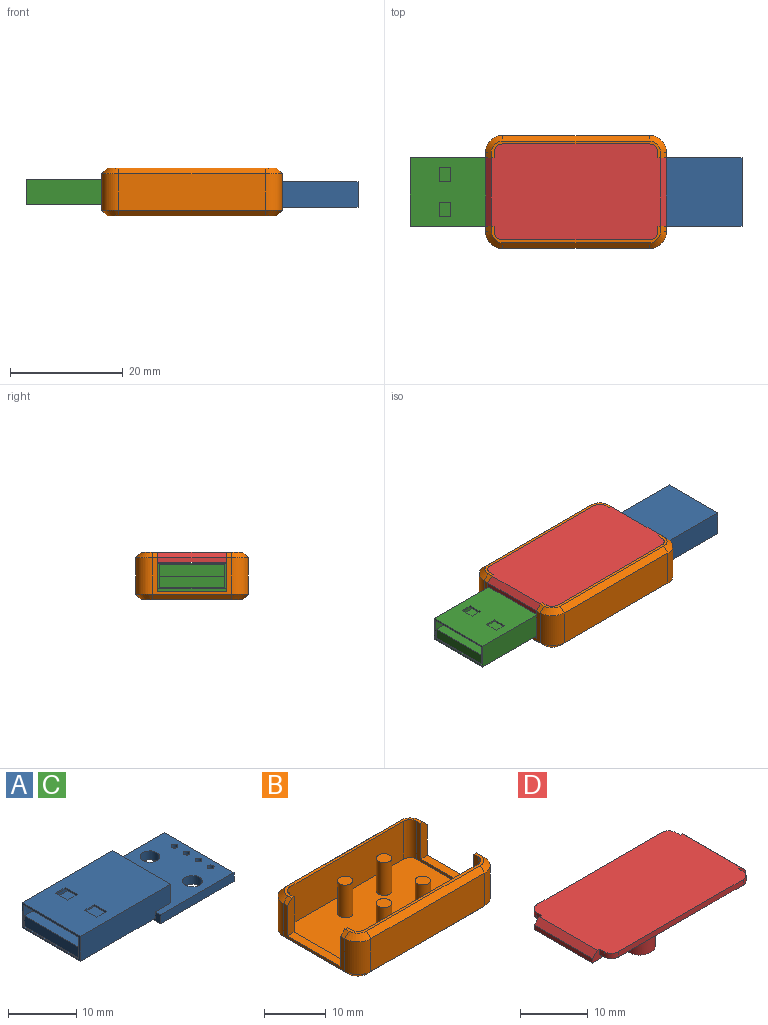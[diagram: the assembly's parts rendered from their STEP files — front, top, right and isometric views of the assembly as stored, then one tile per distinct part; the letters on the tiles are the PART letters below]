
ASSEMBLY  parts=4 mates=3
PART A: 33 faces, bbox 30.8x14.4x5 mm
  f0: plane 18.8x12.14mm, normal (0,0,1), area 218.2mm2, adj f2,f3,f4,f5,f25,f26,f27,f28
  f1: plane 17x11.54mm, normal (0,0,-1), area 186.2mm2, adj f2,f20,f21,f24,f25,f26,f27,f28
  f2: plane 12.14x4.5mm, normal (-1,0,0), area 9.6mm2, adj f0,f1,f3,f5,f6,f19,f20,f21
  f3: plane 18.8x4.5mm, normal (0,-1,0), area 80.9mm2, adj f0,f2,f4,f6,f8,f18
  f4: plane 12.14x3.35mm, normal (1,0,0), area 40.7mm2, adj f0,f3,f5,f18
  f5: plane 18.8x4.5mm, normal (0,1,0), area 80.9mm2, adj f0,f2,f4,f6,f8,f18
  f6: plane 15.56x12.14mm, normal (0,0,-1), area 188.9mm2, adj f2,f3,f5,f8
  f7: plane 15.24x1.6mm, normal (0,1,0), area 24.4mm2, adj f8,f15,f17,f18
  f8: plane 14.43x1.6mm, normal (-1,0,0), area 9.1mm2, adj f3,f5,f6,f7,f9,f17,f18
  f9: plane 15.24x1.6mm, normal (0,-1,0), area 24.4mm2, adj f8,f15,f17,f18
  f10: cylinder r=0.5mm len=1.6mm, axis (0,0,1), area 5mm2, adj f17,f18
  f11: cylinder r=0.5mm len=1.6mm, axis (0,0,1), area 5mm2, adj f17,f18
  f12: cylinder r=0.5mm len=1.6mm, axis (0,0,1), area 5mm2, adj f17,f18
  f13: cylinder r=1.45mm len=2.9mm, axis (0,0,1), area 14.6mm2, adj f17,f18
  f14: cylinder r=0.5mm len=1.6mm, axis (0,0,1), area 5mm2, adj f17,f18
  f15: plane 14.43x1.6mm, normal (1,0,0), area 23.1mm2, adj f7,f9,f17,f18
  f16: cylinder r=1.45mm len=2.9mm, axis (0,0,1), area 14.6mm2, adj f17,f18
  f17: plane 15.24x14.43mm, normal (0,0,-1), area 203.6mm2, adj f7,f8,f9,f10,f11,f12,f13,f14
  f18: plane 15.24x14.43mm, normal (0,0,1), area 164.2mm2, adj f3,f4,f5,f7,f8,f9,f10,f11
  f19: plane 11.54x0.2mm, normal (0,0,1), area 2.3mm2, adj f2,f20,f21,f22
  f20: plane 17x3.9mm, normal (0,1,0), area 34.4mm2, adj f1,f2,f19,f22,f23,f24
  f21: plane 17x3.9mm, normal (0,-1,0), area 34.4mm2, adj f1,f2,f19,f22,f23,f24
  f22: plane 11.54x1.9mm, normal (-1,0,0), area 21.9mm2, adj f19,f20,f21,f23
  f23: plane 16.8x11.54mm, normal (0,0,1), area 193.9mm2, adj f20,f21,f22,f24
  f24: plane 11.54x2mm, normal (-1,0,0), area 23.1mm2, adj f1,f20,f21,f23
  f25: plane 2.5x0.3mm, normal (-1,0,0), area 0.7mm2, adj f0,f1,f26,f27
  f26: plane 2x0.3mm, normal (0,-1,0), area 0.6mm2, adj f0,f1,f25,f28
  f27: plane 2x0.3mm, normal (0,1,0), area 0.6mm2, adj f0,f1,f25,f28
  f28: plane 2.5x0.3mm, normal (1,0,0), area 0.7mm2, adj f0,f1,f26,f27
  f29: plane 2x0.3mm, normal (0,-1,0), area 0.6mm2, adj f0,f1,f30,f31
  f30: plane 2.5x0.3mm, normal (1,0,0), area 0.7mm2, adj f0,f1,f29,f32
  f31: plane 2.5x0.3mm, normal (-1,0,0), area 0.7mm2, adj f0,f1,f29,f32
  f32: plane 2x0.3mm, normal (0,1,0), area 0.6mm2, adj f0,f1,f30,f31
PART B: 52 faces, bbox 32x20x8.5 mm
  f0: plane 30x2.93mm, normal (0,0,1), area 16.7mm2, adj f2,f8,f9,f11,f21,f29,f33,f39
  f1: plane 14x6.5mm, normal (1,0,0), area 18.2mm2, adj f20,f24,f28,f29,f30,f38,f39,f48
  f2: plane 14x7.5mm, normal (-1,0,0), area 20mm2, adj f0,f3,f10,f21,f25,f28,f29,f30
  f3: plane 29x17mm, normal (0,0,1), area 471.4mm2, adj f2,f8,f9,f11,f12,f16,f17,f18
  f4: plane 26x6.5mm, normal (0,-1,0), area 169mm2, adj f5,f20,f41,f44
  f5: cylinder r=3mm len=6.5mm, axis (0,0,1), area 30.6mm2, adj f4,f6,f42,f45
  f6: plane 14x6.5mm, normal (-1,0,0), area 18.2mm2, adj f5,f15,f31,f32,f33,f34,f43,f47
  f7: plane 30x18mm, normal (0,0,-1), area 536.6mm2, adj f44,f45,f46,f47,f48,f49,f50,f51
  f8: plane 14x7.5mm, normal (1,0,0), area 20mm2, adj f0,f3,f9,f10,f16,f31,f32,f33
  f9: cylinder r=1.5mm len=7.5mm, axis (0,0,1), area 17.7mm2, adj f0,f3,f8,f11
  f10: plane 30x2.93mm, normal (0,0,1), area 16.7mm2, adj f2,f8,f16,f17,f25,f30,f32,f34
  f11: plane 26x7.5mm, normal (0,1,0), area 195mm2, adj f0,f3,f9,f21
  f12: cylinder r=1.25mm len=6.5mm, axis (0,0,-1), area 51.1mm2, adj f3,f13
  f13: plane 2.5x2.5mm, normal (0,0,1), area 4.9mm2, adj f12
  f14: plane 26x6.5mm, normal (0,1,0), area 169mm2, adj f15,f24,f36,f51
  f15: cylinder r=3mm len=6.5mm, axis (0,0,1), area 30.6mm2, adj f6,f14,f35,f49
  f16: cylinder r=1.5mm len=7.5mm, axis (0,0,1), area 17.7mm2, adj f3,f8,f10,f17
  f17: plane 26x7.5mm, normal (0,-1,0), area 195mm2, adj f3,f10,f16,f25
  f18: cylinder r=1.25mm len=6.5mm, axis (0,0,-1), area 51.1mm2, adj f3,f19
  f19: plane 2.5x2.5mm, normal (0,0,1), area 4.9mm2, adj f18
  f20: cylinder r=3mm len=6.5mm, axis (0,0,1), area 30.6mm2, adj f1,f4,f40,f46
  f21: cylinder r=1.5mm len=7.5mm, axis (0,0,1), area 17.7mm2, adj f0,f2,f3,f11
  f22: cylinder r=1.25mm len=6.5mm, axis (0,0,-1), area 51.1mm2, adj f3,f23
  f23: plane 2.5x2.5mm, normal (0,0,1), area 4.9mm2, adj f22
  f24: cylinder r=3mm len=6.5mm, axis (0,0,1), area 30.6mm2, adj f1,f14,f37,f50
  f25: cylinder r=1.5mm len=7.5mm, axis (0,0,1), area 17.7mm2, adj f2,f3,f10,f17
  f26: cylinder r=1.25mm len=6.5mm, axis (0,0,-1), area 51.1mm2, adj f3,f27
  f27: plane 2.5x2.5mm, normal (0,0,1), area 4.9mm2, adj f26
  f28: plane 12.14x1.5mm, normal (0,0,1), area 18.2mm2, adj f1,f2,f29,f30
  f29: plane 7x1.5mm, normal (0,1,0), area 10mm2, adj f0,f1,f2,f28,f39
  f30: plane 7x1.5mm, normal (0,-1,0), area 10mm2, adj f1,f2,f10,f28,f38
  f31: plane 12.14x1.5mm, normal (0,0,1), area 18.2mm2, adj f6,f8,f32,f33
  f32: plane 7x1.5mm, normal (0,-1,0), area 10mm2, adj f6,f8,f10,f31,f34
  f33: plane 7x1.5mm, normal (0,1,0), area 10mm2, adj f0,f6,f8,f31,f43
  f34: plane 1x1mm, normal (-0.71,0,0.71), area 1.3mm2, adj f6,f10,f32,f35
  f35: cone r=2mm half-angle=45deg, axis (0,0,-1), area 5.6mm2, adj f10,f15,f34,f36
  f36: plane 26x1mm, normal (0,0.71,0.71), area 36.8mm2, adj f10,f14,f35,f37
  f37: cone r=3mm half-angle=45deg, axis (0,0,-1), area 5.6mm2, adj f10,f24,f36,f38
  f38: plane 1x1mm, normal (0.71,0,0.71), area 1.3mm2, adj f1,f10,f30,f37
  f39: plane 1x1mm, normal (0.71,0,0.71), area 1.3mm2, adj f0,f1,f29,f40
  f40: cone r=2mm half-angle=45deg, axis (0,0,-1), area 5.6mm2, adj f0,f20,f39,f41
  f41: plane 26x1mm, normal (0,-0.71,0.71), area 36.8mm2, adj f0,f4,f40,f42
  f42: cone r=3mm half-angle=45deg, axis (0,0,-1), area 5.6mm2, adj f0,f5,f41,f43
  f43: plane 1x1mm, normal (-0.71,0,0.71), area 1.3mm2, adj f0,f6,f33,f42
  f44: plane 26x1mm, normal (0,-0.71,-0.71), area 36.8mm2, adj f4,f7,f45,f46
  f45: cone r=2mm half-angle=45deg, axis (0,0,1), area 5.6mm2, adj f5,f7,f44,f47
  f46: cone r=3mm half-angle=45deg, axis (0,0,1), area 5.6mm2, adj f7,f20,f44,f48
  f47: plane 14x1mm, normal (-0.71,0,-0.71), area 19.8mm2, adj f6,f7,f45,f49
  f48: plane 14x1mm, normal (0.71,0,-0.71), area 19.8mm2, adj f1,f7,f46,f50
  f49: cone r=3mm half-angle=45deg, axis (0,0,1), area 5.6mm2, adj f7,f15,f47,f51
  f50: cone r=2mm half-angle=45deg, axis (0,0,1), area 5.6mm2, adj f7,f24,f48,f51
  f51: plane 26x1mm, normal (0,0.71,-0.71), area 36.8mm2, adj f7,f14,f49,f50
PART C: same geometry as A
PART D: 42 faces, bbox 32x17x5.4 mm
  f0: plane 1x0.93mm, normal (-1,0,0), area 0.9mm2, adj f1,f3,f5,f7
  f1: plane 30x17mm, normal (0,0,1), area 503.2mm2, adj f0,f4,f5,f7,f9,f11,f12,f13
  f2: cylinder r=2.25mm len=4.5mm, axis (0,0,1), area 47.4mm2, adj f30,f38
  f3: plane 29x17mm, normal (0,0,-1), area 334.1mm2, adj f0,f4,f5,f7,f9,f11,f12,f13
  f4: plane 26x1mm, normal (0,1,0), area 26mm2, adj f1,f3,f5,f17
  f5: cylinder r=1.5mm len=1.5mm, axis (0,0,1), area 2.4mm2, adj f0,f1,f3,f4
  f6: plane 12.14x1.7mm, normal (0,0,-1), area 20.6mm2, adj f7,f8,f13,f41
  f7: plane 2.5x1.8mm, normal (0,1,0), area 2.7mm2, adj f0,f1,f3,f6,f8,f28,f41
  f8: plane 12.14x0.8mm, normal (-1,0,0), area 9.7mm2, adj f6,f7,f13,f28
  f9: plane 1x0.93mm, normal (-1,0,0), area 0.9mm2, adj f1,f3,f12,f13
  f10: cylinder r=2.25mm len=4.5mm, axis (0,0,1), area 47.4mm2, adj f33,f37
  f11: plane 26x1mm, normal (0,-1,0), area 26mm2, adj f1,f3,f12,f25
  f12: cylinder r=1.5mm len=1.5mm, axis (0,0,1), area 2.4mm2, adj f1,f3,f9,f11
  f13: plane 2.5x1.8mm, normal (0,-1,0), area 2.7mm2, adj f1,f3,f6,f8,f9,f28,f41
  f14: plane 1x0.93mm, normal (1,0,0), area 0.9mm2, adj f1,f3,f17,f20
  f15: plane 4.5x4.5mm, normal (0,0,-1), area 11mm2, adj f16,f39
  f16: cylinder r=1.25mm len=2.5mm, axis (0,0,1), area 7.9mm2, adj f15,f18
  f17: cylinder r=1.5mm len=1.5mm, axis (0,0,1), area 2.4mm2, adj f1,f3,f4,f14
  f18: plane 2.5x2.5mm, normal (0,0,-1), area 4.9mm2, adj f16
  f19: plane 12.14x1.7mm, normal (0,0,-1), area 20.6mm2, adj f20,f21,f27,f40
  f20: plane 2.5x1.8mm, normal (0,1,0), area 2.7mm2, adj f1,f3,f14,f19,f21,f29,f40
  f21: plane 12.14x0.8mm, normal (1,0,0), area 9.7mm2, adj f19,f20,f27,f29
  f22: plane 1x0.93mm, normal (1,0,0), area 0.9mm2, adj f1,f3,f25,f27
  f23: plane 4.5x4.5mm, normal (0,0,-1), area 11mm2, adj f24,f36
  f24: cylinder r=1.25mm len=2.5mm, axis (0,0,1), area 7.9mm2, adj f23,f26
  f25: cylinder r=1.5mm len=1.5mm, axis (0,0,1), area 2.4mm2, adj f1,f3,f11,f22
  f26: plane 2.5x2.5mm, normal (0,0,-1), area 4.9mm2, adj f24
  f27: plane 2.5x1.8mm, normal (0,-1,0), area 2.7mm2, adj f1,f3,f19,f21,f22,f29,f40
  f28: plane 12.14x1mm, normal (-0.71,0,0.71), area 17.2mm2, adj f1,f7,f8,f13
  f29: plane 12.14x1mm, normal (0.71,0,0.71), area 17.2mm2, adj f1,f20,f21,f27
  f30: plane 4.5x4.5mm, normal (0,0,-1), area 11mm2, adj f2,f32
  f31: plane 2.5x2.5mm, normal (0,0,-1), area 4.9mm2, adj f32
  f32: cylinder r=1.25mm len=4.35mm, axis (0,0,1), area 34.2mm2, adj f30,f31
  f33: plane 4.5x4.5mm, normal (0,0,-1), area 11mm2, adj f10,f35
  f34: plane 2.5x2.5mm, normal (0,0,-1), area 4.9mm2, adj f35
  f35: cylinder r=1.25mm len=4.35mm, axis (0,0,1), area 34.2mm2, adj f33,f34
  f36: cone r=3.25mm half-angle=45deg, axis (0,0,1), area 24.4mm2, adj f3,f23
  f37: cone r=2.25mm half-angle=45deg, axis (0,0,1), area 24.4mm2, adj f3,f10
  f38: cone r=3.25mm half-angle=45deg, axis (0,0,1), area 24.4mm2, adj f2,f3
  f39: cone r=2.25mm half-angle=45deg, axis (0,0,1), area 24.4mm2, adj f3,f15
  f40: plane 12.14x0.8mm, normal (-0.71,0,-0.71), area 13.7mm2, adj f3,f19,f20,f27
  f41: plane 12.14x0.8mm, normal (0.71,0,-0.71), area 13.7mm2, adj f3,f6,f7,f13
PLACE A rot(axis=(0,1,0),180deg) t=(32.88,4.49,9.73)mm
PLACE B t=(-7.12,4.49,5.63)mm
PLACE C t=(-7.12,4.49,5.68)mm
PLACE D t=(-7.12,4.49,5.63)mm
MATE fastened B.f26 <-> A.f16  axis (0,0,1) through (17.33,8.91,11.18)mm
MATE fastened A.f14 <-> C.f14  axis (0,0,-1) through (12.88,0.74,8.58)mm
MATE fastened D.f16 <-> B.f26  axis (0,0,1) through (17.33,8.91,10.68)mm
